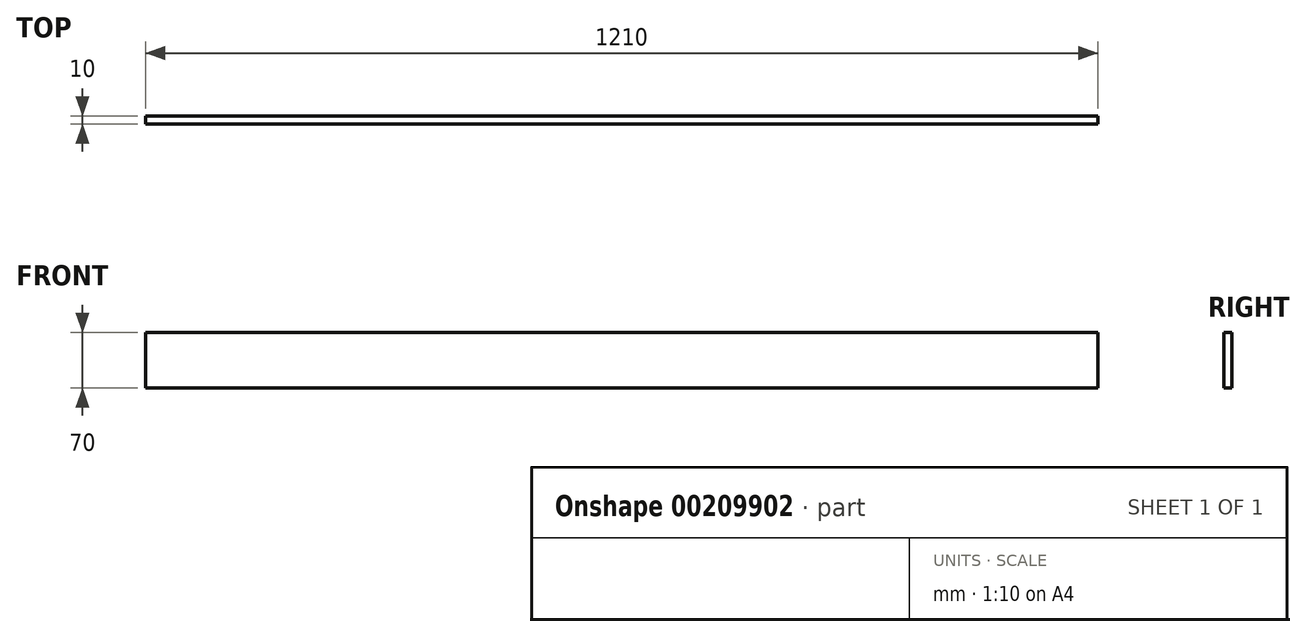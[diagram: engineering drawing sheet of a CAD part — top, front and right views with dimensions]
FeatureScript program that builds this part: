
annotation { "Feature Type Name" : "Feature", "Feature Type Description" : "" }
export const myFeature = defineFeature(function(context is Context, id is Id, definition is map)
    precondition{}
    {
        {
            var Q0;
            Q0=qCreatedBy(makeId("Front.planeOp"),FACE);
            var sketch = newSketch(context, id + "F0", { "sketchPlane" : qUnion([Q0])});
            skLineSegment(sketch, "E0.bottom", {"start": v(-605, 35) * mm, "end": v(605, 35) * mm});
            skLineSegment(sketch, "E0.top", {"start": v(-605, -35) * mm, "end": v(605, -35) * mm});
            skLineSegment(sketch, "E0.left", {"start": v(-605, 35) * mm, "end": v(-605, -35) * mm});
            skLineSegment(sketch, "E0.right", {"start": v(605, 35) * mm, "end": v(605, -35) * mm});
            skPoint(sketch, "E0.middle", {"position": v(0, 0) * mm});
            skSolve(sketch);
        }
        {
            var Q0;
            Q0=makeQuery(id+"F0.imprint","IMPRINT",FACE,{"disambiguationData":[TD([[makeQuery(id+"F0.imprint","IMPRINT",EDGE,{"derivedFrom":sQuery(id+"F0.wireOp",EDGE,"E0.bottom")}),-1.0]])]});
            extrude(context, id + "F1", {"entities" : qUnion([Q0]), "depth" : 10 * mm});
        }
    });
